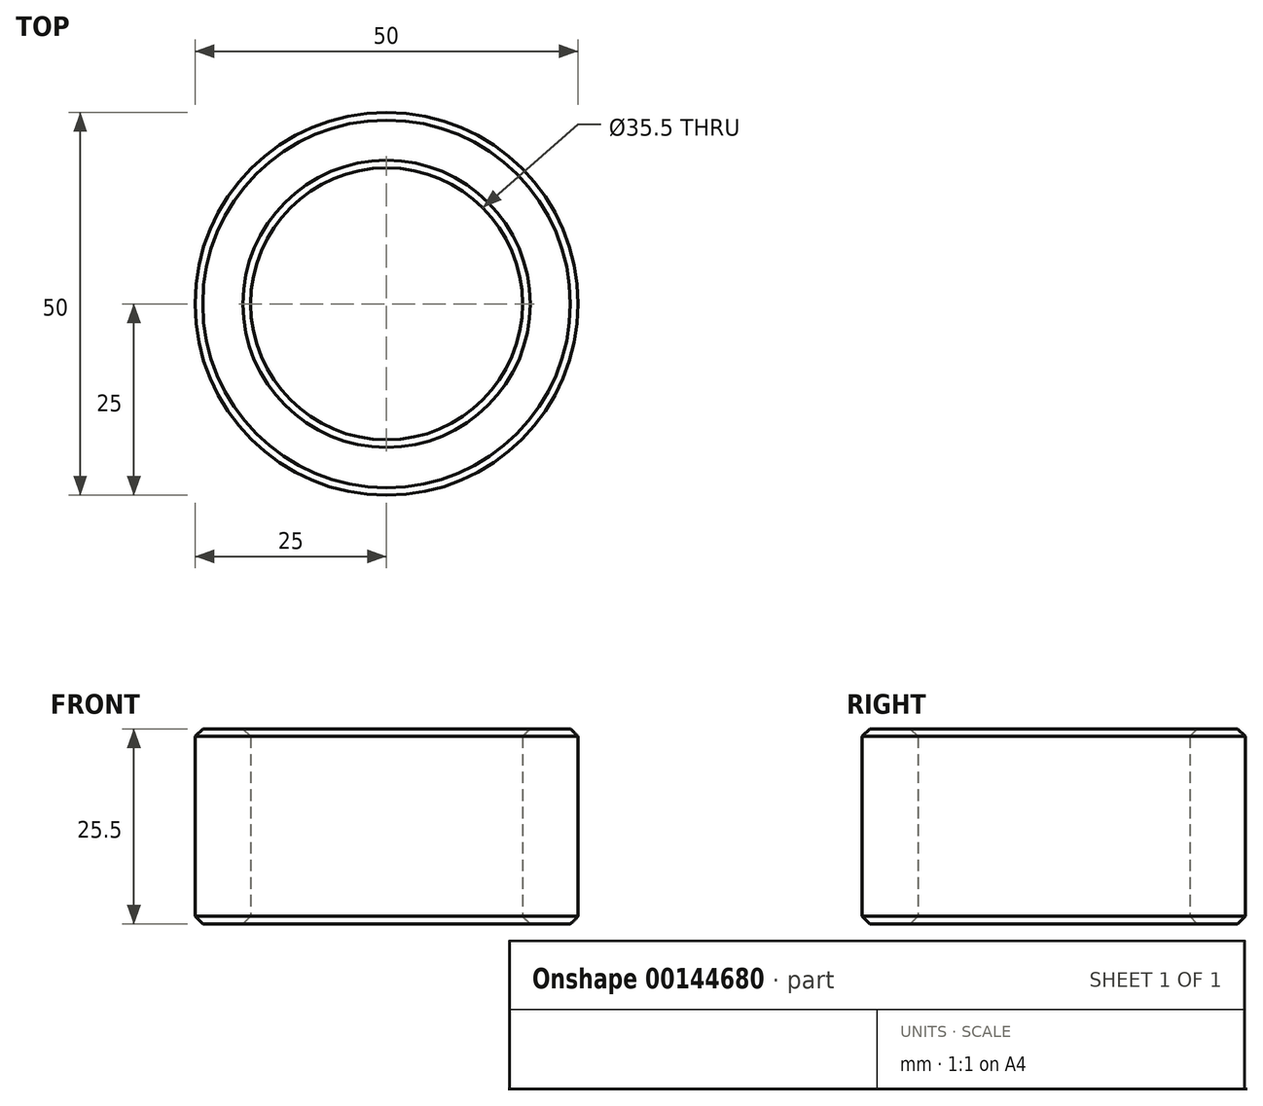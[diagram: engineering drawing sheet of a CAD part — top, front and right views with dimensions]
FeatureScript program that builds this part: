
annotation { "Feature Type Name" : "Feature", "Feature Type Description" : "" }
export const myFeature = defineFeature(function(context is Context, id is Id, definition is map)
    precondition{}
    {
        {
            var Q0;
            Q0=qCreatedBy(makeId("Top.planeOp"),FACE);
            var sketch = newSketch(context, id + "F0", { "sketchPlane" : qUnion([Q0])});
            skCircle(sketch, "E0", {"center": v(0, 0) * mm, "radius": 25 * mm});
            skCircle(sketch, "E1", {"center": v(0, 0) * mm, "radius": 17.75 * mm});
            skSolve(sketch);
        }
        {
            var Q0;
            Q0 = qSketchRegion(id + "F0", true);
            extrude(context, id + "F1", {"entities" : qUnion([Q0]), "endBound" : BoundingType.SYMMETRIC, "depth" : 25.5 * mm});
        }
        {
            var Q0;
            Q0=makeQuery(id+"F1.opExtrude","CAP_FACE",FACE,{"disambiguationData":[OSD([sQuery(id+"F0.wireOp",EDGE,"E0"),sQuery(id+"F0.wireOp",EDGE,"E1")])],"isStart":false});
            var Q1;
            Q1=makeQuery(id+"F1.opExtrude","CAP_FACE",FACE,{"disambiguationData":[OSD([sQuery(id+"F0.wireOp",EDGE,"E0"),sQuery(id+"F0.wireOp",EDGE,"E1")])],"isStart":true});
            chamfer(context, id + "F2", {"entities" : qUnion([Q0, Q1]), "width" : 1 * mm, "tangentPropagation" : true});
        }
    });
